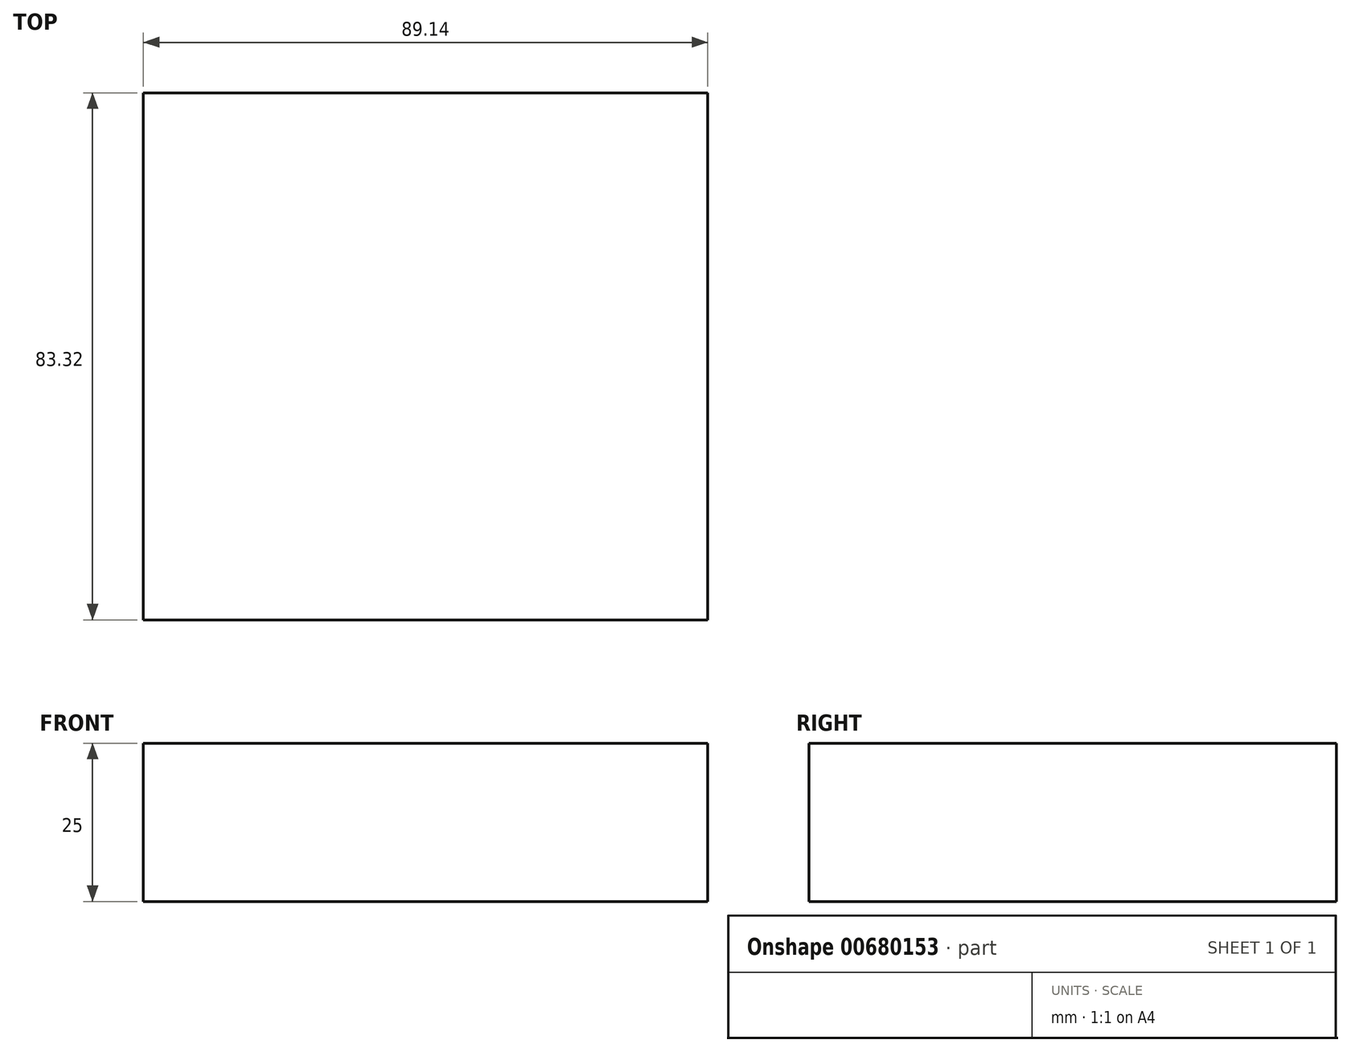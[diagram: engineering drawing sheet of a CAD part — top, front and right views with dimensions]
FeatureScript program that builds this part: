
annotation { "Feature Type Name" : "Feature", "Feature Type Description" : "" }
export const myFeature = defineFeature(function(context is Context, id is Id, definition is map)
    precondition{}
    {
        {
            var Q0;
            Q0=qCreatedBy(makeId("Top.planeOp"),FACE);
            var sketch = newSketch(context, id + "F0", { "sketchPlane" : qUnion([Q0])});
            skLineSegment(sketch, "E0.bottom", {"start": v(44.57, -41.66) * mm, "end": v(-44.57, -41.66) * mm});
            skLineSegment(sketch, "E0.top", {"start": v(44.57, 41.66) * mm, "end": v(-44.57, 41.66) * mm});
            skLineSegment(sketch, "E0.left", {"start": v(44.57, -41.66) * mm, "end": v(44.57, 41.66) * mm});
            skLineSegment(sketch, "E0.right", {"start": v(-44.57, -41.66) * mm, "end": v(-44.57, 41.66) * mm});
            skPoint(sketch, "E0.middle", {"position": v(0, 0) * mm});
            skSolve(sketch);
        }
        {
            var Q0;
            Q0 = qSketchRegion(id + "F0", true);
            extrude(context, id + "F1", {"entities" : qUnion([Q0]), "depth" : 25 * mm, "offsetDistance" : 25 * mm});
        }
    });
